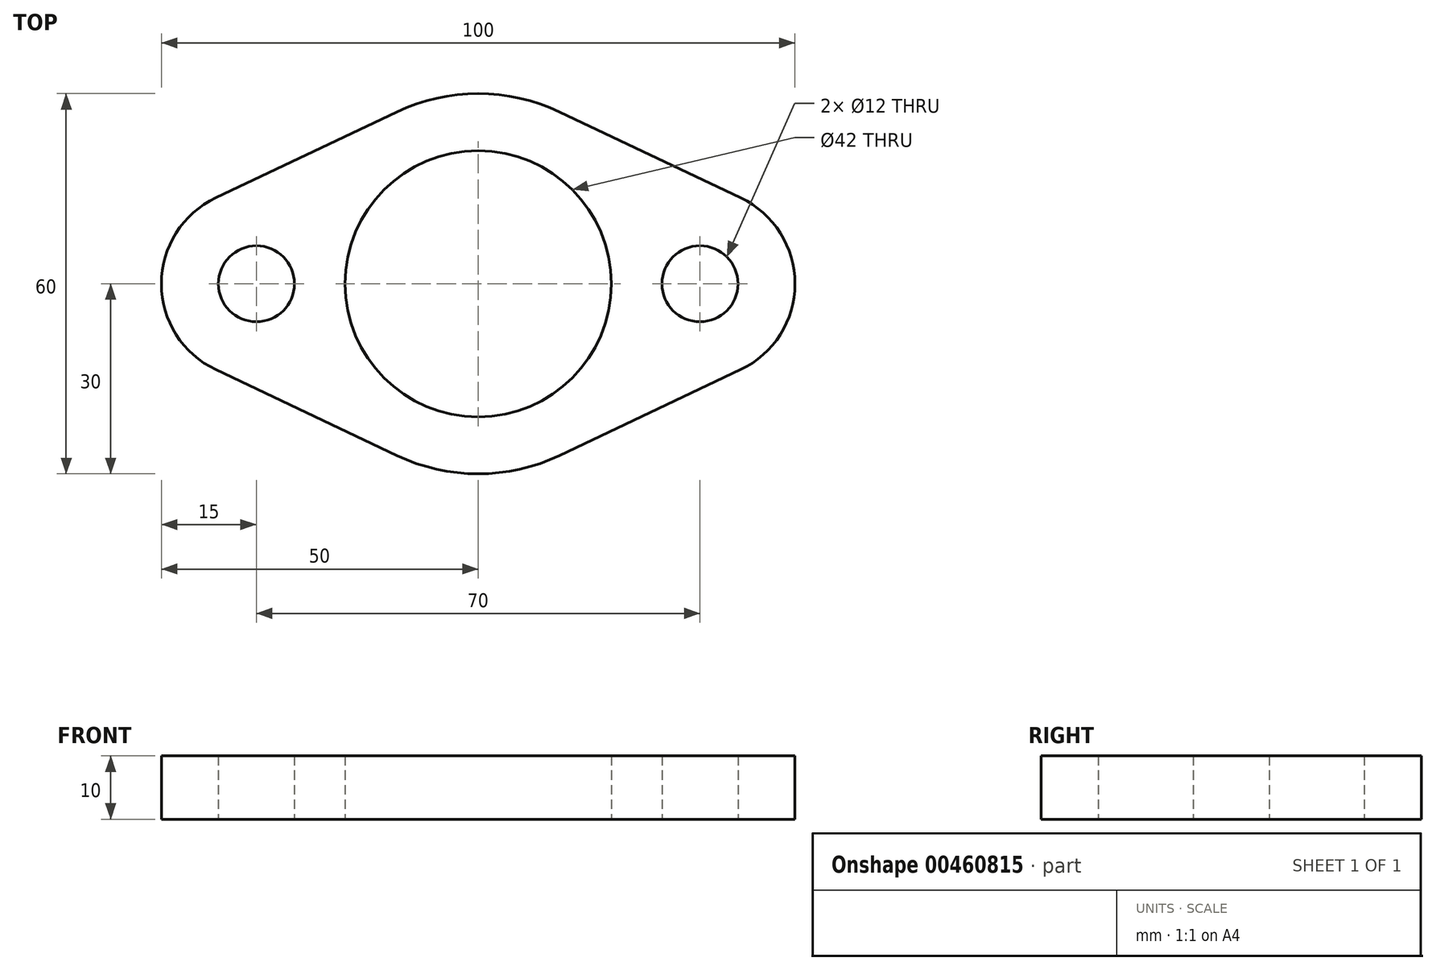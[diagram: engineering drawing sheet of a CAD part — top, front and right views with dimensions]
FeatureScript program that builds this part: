
annotation { "Feature Type Name" : "Feature", "Feature Type Description" : "" }
export const myFeature = defineFeature(function(context is Context, id is Id, definition is map)
    precondition{}
    {
        {
            var Q0;
            Q0=qCreatedBy(makeId("Top.planeOp"),FACE);
            var sketch = newSketch(context, id + "F0", { "sketchPlane" : qUnion([Q0])});
            skCircle(sketch, "E0", {"center": v(0, 0) * mm, "radius": 21 * mm});
            skCircle(sketch, "E1", {"center": v(-35, 0) * mm, "radius": 6 * mm});
            skCircle(sketch, "E2", {"center": v(35, 0) * mm, "radius": 6 * mm});
            skArc(sketch, "E3", {"start": v(-41.43, 13.55) * mm, "mid": v(-50, 0) * mm, "end": v(-41.43, -13.55) * mm});
            skLineSegment(sketch, "E4", {"start": v(-41.43, 13.55) * mm, "end": v(-12.86, 27.1) * mm});
            skLineSegment(sketch, "E5", {"start": v(-41.43, -13.55) * mm, "end": v(-12.86, -27.1) * mm});
            skLineSegment(sketch, "E6", {"start": v(12.86, 27.1) * mm, "end": v(41.43, 13.55) * mm});
            skLineSegment(sketch, "E7", {"start": v(12.86, -27.1) * mm, "end": v(41.43, -13.55) * mm});
            skPoint(sketch, "E8.orphan", {"position": v(0, -33.2) * mm});
            skArc(sketch, "E9.trimOffspring", {"start": v(-12.86, -27.1) * mm, "mid": v(0, -30) * mm, "end": v(12.86, -27.1) * mm});
            skArc(sketch, "E10.trimOffspring", {"start": v(41.43, -13.55) * mm, "mid": v(50, 0) * mm, "end": v(41.43, 13.55) * mm});
            skArc(sketch, "E11.trimOffspring", {"start": v(12.86, 27.1) * mm, "mid": v(0, 30) * mm, "end": v(-12.86, 27.1) * mm});
            skSolve(sketch);
        }
        {
            var Q0;
            Q0=makeQuery(id+"F0.imprint","IMPRINT",FACE,{"disambiguationData":[TD([[makeQuery(id+"F0.imprint","IMPRINT",EDGE,{"derivedFrom":sQuery(id+"F0.wireOp",EDGE,"E0")}),-1.0]])]});
            extrude(context, id + "F1", {"entities" : qUnion([Q0]), "depth" : 10 * mm});
        }
    });
